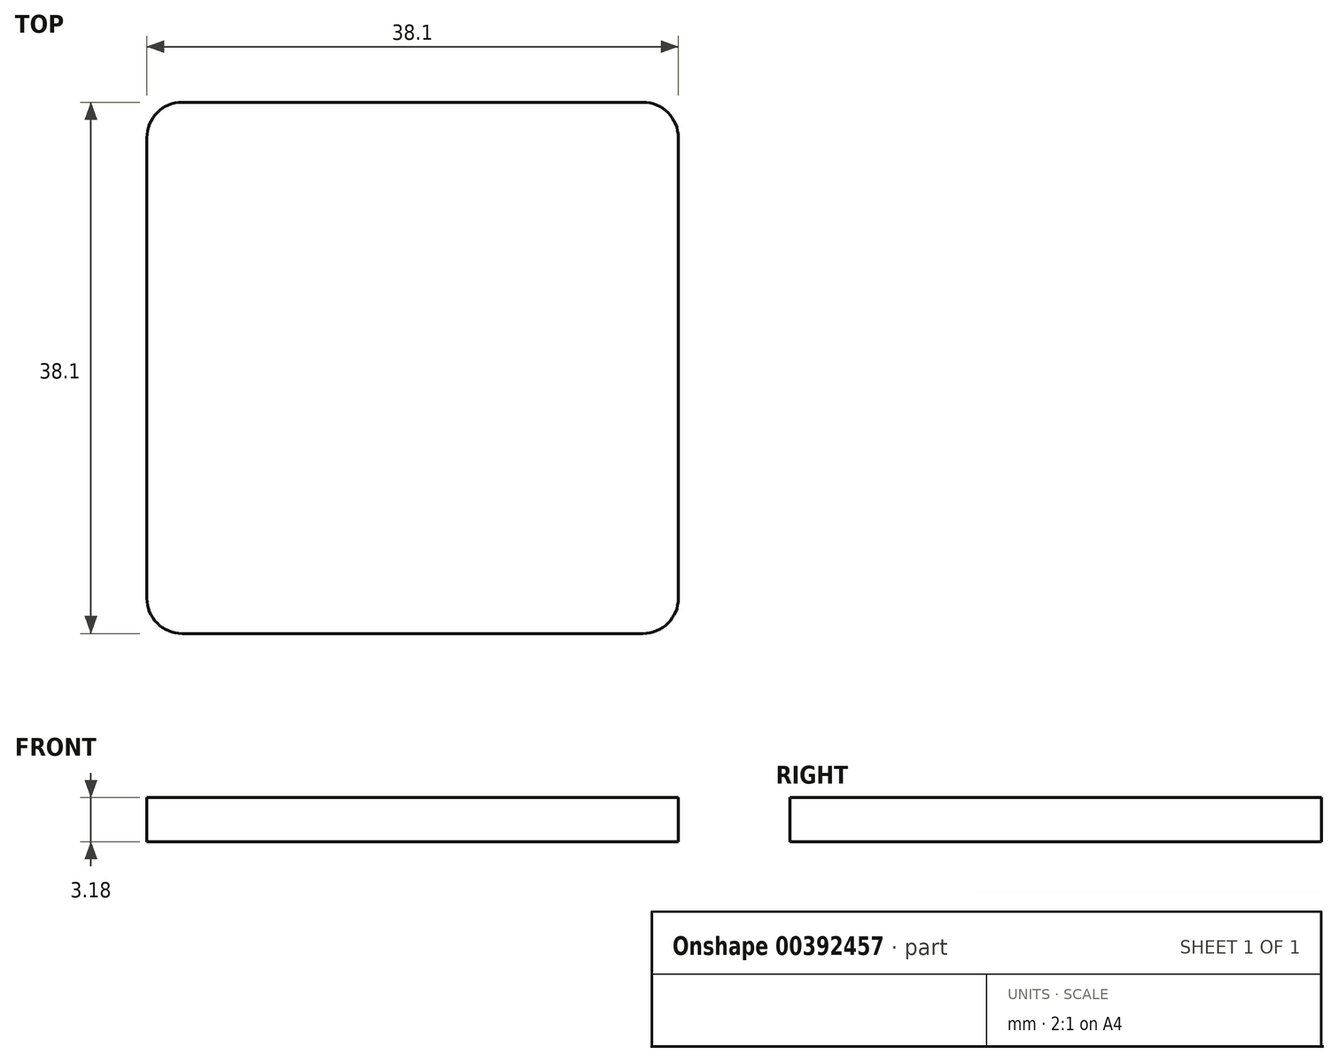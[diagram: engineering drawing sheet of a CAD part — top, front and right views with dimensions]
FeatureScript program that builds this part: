
annotation { "Feature Type Name" : "Feature", "Feature Type Description" : "" }
export const myFeature = defineFeature(function(context is Context, id is Id, definition is map)
    precondition{}
    {
        {
            var Q0;
            Q0=qCreatedBy(makeId("Front.planeOp"),FACE);
            var sketch = newSketch(context, id + "F0", { "sketchPlane" : qUnion([Q0])});
            skLineSegment(sketch, "E0.bottom", {"start": v(-18.97, 1.59) * mm, "end": v(19.13, 1.59) * mm});
            skLineSegment(sketch, "E0.top", {"start": v(-18.97, -1.59) * mm, "end": v(19.13, -1.59) * mm});
            skLineSegment(sketch, "E0.left", {"start": v(-18.97, 1.59) * mm, "end": v(-18.97, -1.59) * mm});
            skLineSegment(sketch, "E0.right", {"start": v(19.13, 1.59) * mm, "end": v(19.13, -1.59) * mm});
            skPoint(sketch, "E0.middle", {"position": v(0.08, 0) * mm});
            skSolve(sketch);
        }
        {
            var Q0;
            Q0=makeQuery(id+"F0.imprint","IMPRINT",FACE,{"disambiguationData":[TD([[makeQuery(id+"F0.imprint","IMPRINT",EDGE,{"derivedFrom":sQuery(id+"F0.wireOp",EDGE,"E0.bottom")}),-1.0]])]});
            extrude(context, id + "F1", {"entities" : qUnion([Q0]), "depth" : 38.1 * mm});
        }
        {
            var Q0;
            Q0=makeQuery(id+"F1.opExtrude","CAP_EDGE",EDGE,{"disambiguationData":[OSD([sQuery(id+"F0.wireOp",EDGE,"E0.right")])],"isStart":false});
            var Q1;
            Q1=makeQuery(id+"F1.opExtrude","CAP_EDGE",EDGE,{"disambiguationData":[OSD([sQuery(id+"F0.wireOp",EDGE,"E0.left")])],"isStart":false});
            var Q2;
            Q2=makeQuery(id+"F1.opExtrude","CAP_EDGE",EDGE,{"disambiguationData":[OSD([sQuery(id+"F0.wireOp",EDGE,"E0.left")])],"isStart":true});
            var Q3;
            Q3=makeQuery(id+"F1.opExtrude","CAP_EDGE",EDGE,{"disambiguationData":[OSD([sQuery(id+"F0.wireOp",EDGE,"E0.right")])],"isStart":true});
            fillet(context, id + "F2", {"entities" : qUnion([Q0, Q1, Q2, Q3]), "radius" : 2.54 * mm, "tangentPropagation" : true, "allowEdgeOverflow" : false});
        }
    });
